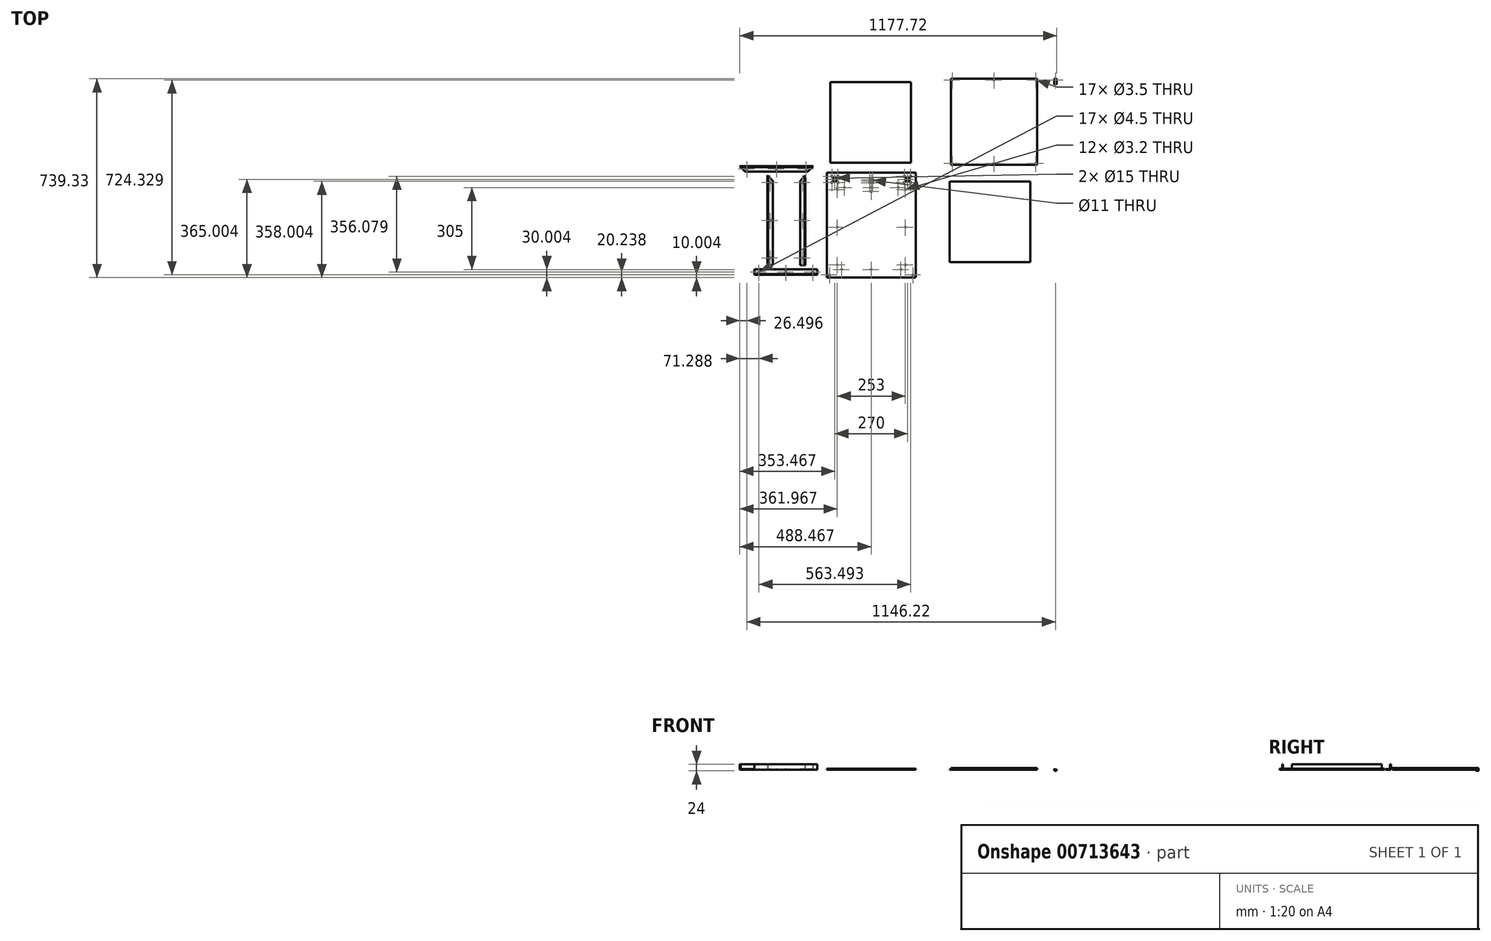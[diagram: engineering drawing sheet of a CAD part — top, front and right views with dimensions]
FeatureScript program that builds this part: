
annotation { "Feature Type Name" : "Feature", "Feature Type Description" : "" }
export const myFeature = defineFeature(function(context is Context, id is Id, definition is map)
    precondition{}
    {
        {
            var Q0;
            Q0=qCreatedBy(makeId("Top.planeOp"),FACE);
            var sketch = newSketch(context, id + "F0", { "sketchPlane" : qUnion([Q0])});
            skLineSegment(sketch, "E0.bottom", {"start": v(150, 187.33) * mm, "end": v(480, 187.33) * mm});
            skLineSegment(sketch, "E0.top", {"start": v(150, -202.67) * mm, "end": v(480, -202.67) * mm});
            skLineSegment(sketch, "E0.left", {"start": v(150, 187.33) * mm, "end": v(150, -202.67) * mm});
            skLineSegment(sketch, "E0.right", {"start": v(480, 187.33) * mm, "end": v(480, -202.67) * mm});
            skCircle(sketch, "E1", {"center": v(180, 162.33) * mm, "radius": 7.5 * mm});
            skCircle(sketch, "E2", {"center": v(450, 162.33) * mm, "radius": 7.5 * mm});
            skCircle(sketch, "E3", {"center": v(315, 155.33) * mm, "radius": 5.5 * mm});
            skPoint(sketch, "E3.centerSnap0", {"position": v(315, 187.33) * mm});
            skLineSegment(sketch, "E4", {"start": v(150, -202.67) * mm, "end": v(480, 187.33) * mm, "construction": true});
            skLineSegment(sketch, "E5.bottom", {"start": v(470, -192.67) * mm, "end": v(160, -192.67) * mm, "construction": true});
            skLineSegment(sketch, "E5.top", {"start": v(470, 117.33) * mm, "end": v(160, 117.33) * mm, "construction": true});
            skLineSegment(sketch, "E5.left", {"start": v(470, -192.67) * mm, "end": v(470, 117.33) * mm, "construction": true});
            skLineSegment(sketch, "E5.right", {"start": v(160, -192.67) * mm, "end": v(160, 117.33) * mm, "construction": true});
            skPoint(sketch, "E5.middle", {"position": v(315, -37.67) * mm});
            skCircle(sketch, "E6", {"center": v(315, 117.33) * mm, "radius": 1.75 * mm});
            skCircle(sketch, "E7", {"center": v(160, -192.67) * mm, "radius": 1.75 * mm});
            skCircle(sketch, "E8", {"center": v(470, -192.67) * mm, "radius": 1.75 * mm});
            skLineSegment(sketch, "E9", {"start": v(315, -7.67) * mm, "end": v(315, -37.67) * mm, "construction": true});
            skLineSegment(sketch, "E10", {"start": v(315, -37.67) * mm, "end": v(315, -37.67) * mm});
            skCircle(sketch, "E11", {"center": v(180, 162.33) * mm, "radius": 16 * mm, "construction": true});
            skCircle(sketch, "E12", {"center": v(168.7, 151.02) * mm, "radius": 2.25 * mm});
            skCircle(sketch, "E13", {"center": v(168.7, 173.65) * mm, "radius": 2.25 * mm});
            skCircle(sketch, "E14", {"center": v(191.32, 173.65) * mm, "radius": 2.25 * mm});
            skCircle(sketch, "E15", {"center": v(191.32, 151.02) * mm, "radius": 2.25 * mm});
            skLineSegment(sketch, "E16.bottom", {"start": v(168.7, 173.65) * mm, "end": v(191.32, 173.65) * mm, "construction": true});
            skLineSegment(sketch, "E16.top", {"start": v(168.7, 151.02) * mm, "end": v(191.32, 151.02) * mm, "construction": true});
            skLineSegment(sketch, "E16.left", {"start": v(168.7, 173.65) * mm, "end": v(168.7, 151.02) * mm, "construction": true});
            skLineSegment(sketch, "E16.right", {"start": v(191.32, 173.65) * mm, "end": v(191.32, 151.02) * mm, "construction": true});
            skCircle(sketch, "E17", {"center": v(450, 162.33) * mm, "radius": 16 * mm, "construction": true});
            skLineSegment(sketch, "E18.bottom", {"start": v(438.7, 173.65) * mm, "end": v(461.32, 173.65) * mm, "construction": true});
            skLineSegment(sketch, "E18.top", {"start": v(438.7, 151.02) * mm, "end": v(461.32, 151.02) * mm, "construction": true});
            skLineSegment(sketch, "E18.left", {"start": v(438.7, 173.65) * mm, "end": v(438.7, 151.02) * mm, "construction": true});
            skLineSegment(sketch, "E18.right", {"start": v(461.32, 173.65) * mm, "end": v(461.32, 151.02) * mm, "construction": true});
            skCircle(sketch, "E19", {"center": v(438.7, 173.65) * mm, "radius": 2.25 * mm});
            skCircle(sketch, "E20", {"center": v(461.32, 173.65) * mm, "radius": 2.25 * mm});
            skCircle(sketch, "E21", {"center": v(461.32, 151.02) * mm, "radius": 2.25 * mm});
            skCircle(sketch, "E22", {"center": v(438.7, 151.02) * mm, "radius": 2.25 * mm});
            skCircle(sketch, "E23", {"center": v(315, 155.33) * mm, "radius": 8 * mm, "construction": true});
            skLineSegment(sketch, "E24.bottom", {"start": v(309.35, 161) * mm, "end": v(320.66, 161) * mm, "construction": true});
            skLineSegment(sketch, "E24.top", {"start": v(309.35, 149.68) * mm, "end": v(320.66, 149.68) * mm, "construction": true});
            skLineSegment(sketch, "E24.left", {"start": v(309.35, 161) * mm, "end": v(309.35, 149.68) * mm, "construction": true});
            skLineSegment(sketch, "E24.right", {"start": v(320.66, 161) * mm, "end": v(320.66, 149.68) * mm, "construction": true});
            skCircle(sketch, "E25", {"center": v(309.35, 161) * mm, "radius": 1.75 * mm});
            skCircle(sketch, "E26", {"center": v(320.66, 161) * mm, "radius": 1.75 * mm});
            skCircle(sketch, "E27", {"center": v(320.66, 149.68) * mm, "radius": 1.75 * mm});
            skCircle(sketch, "E28", {"center": v(309.35, 149.68) * mm, "radius": 1.75 * mm});
            skCircle(sketch, "E29", {"center": v(188.5, -155.42) * mm, "radius": 1.6 * mm});
            skCircle(sketch, "E30", {"center": v(315, -172.67) * mm, "radius": 1.6 * mm});
            skPoint(sketch, "E30.centerSnap0", {"position": v(315, -202.67) * mm});
            skCircle(sketch, "E31", {"center": v(205, -172.67) * mm, "radius": 1.6 * mm});
            skCircle(sketch, "E32", {"center": v(425, -172.67) * mm, "radius": 1.6 * mm});
            skCircle(sketch, "E33", {"center": v(441.5, -155.42) * mm, "radius": 1.6 * mm});
            skCircle(sketch, "E34", {"center": v(188.5, -15.42) * mm, "radius": 1.6 * mm});
            skCircle(sketch, "E35", {"center": v(188.5, 124.58) * mm, "radius": 1.6 * mm});
            skCircle(sketch, "E36", {"center": v(441.5, -15.42) * mm, "radius": 1.6 * mm});
            skCircle(sketch, "E37", {"center": v(441.5, 124.58) * mm, "radius": 1.6 * mm});
            skCircle(sketch, "E38", {"center": v(315, 132.33) * mm, "radius": 1.6 * mm});
            skCircle(sketch, "E39", {"center": v(415, 132.33) * mm, "radius": 1.6 * mm});
            skCircle(sketch, "E40", {"center": v(215, 132.33) * mm, "radius": 1.6 * mm});
            skSolve(sketch);
        }
        {
            var Q0;
            Q0=makeQuery(id+"F0.imprint","IMPRINT",FACE,{"disambiguationData":[TD([[makeQuery(id+"F0.imprint","IMPRINT",EDGE,{"derivedFrom":sQuery(id+"F0.wireOp",EDGE,"E0.bottom")}),-1.0]])]});
            extrude(context, id + "F1", {"entities" : qUnion([Q0]), "depth" : 4 * mm});
        }
        {
            var Q0;
            Q0=qCreatedBy(makeId("Top.planeOp"),FACE);
            var sketch = newSketch(context, id + "F2", { "sketchPlane" : qUnion([Q0])});
            skLineSegment(sketch, "E41.bottom", {"start": v(605.69, 155) * mm, "end": v(905.69, 155) * mm});
            skLineSegment(sketch, "E41.top", {"start": v(605.69, -145) * mm, "end": v(905.69, -145) * mm});
            skLineSegment(sketch, "E41.left", {"start": v(605.69, 155) * mm, "end": v(605.69, -145) * mm});
            skLineSegment(sketch, "E41.right", {"start": v(905.69, 155) * mm, "end": v(905.69, -145) * mm});
            skSolve(sketch);
        }
        {
            var Q0;
            Q0=makeQuery(id+"F2.imprint","IMPRINT",FACE,{"disambiguationData":[TD([[makeQuery(id+"F2.imprint","IMPRINT",EDGE,{"derivedFrom":sQuery(id+"F2.wireOp",EDGE,"E41.bottom")}),-1.0]])]});
            extrude(context, id + "F3", {"entities" : qUnion([Q0]), "depth" : 2 * mm});
        }
        {
            var Q0;
            Q0=qCreatedBy(makeId("Top.planeOp"),FACE);
            var sketch = newSketch(context, id + "F4", { "sketchPlane" : qUnion([Q0])});
            skLineSegment(sketch, "E42.bottom", {"start": v(611.16, 536.66) * mm, "end": v(931.16, 536.66) * mm});
            skLineSegment(sketch, "E42.top", {"start": v(611.16, 216.66) * mm, "end": v(931.16, 216.66) * mm});
            skLineSegment(sketch, "E42.left", {"start": v(611.16, 536.66) * mm, "end": v(611.16, 216.66) * mm});
            skLineSegment(sketch, "E42.right", {"start": v(931.16, 536.66) * mm, "end": v(931.16, 216.66) * mm});
            skCircle(sketch, "E43", {"center": v(771.16, 531.66) * mm, "radius": 1.75 * mm});
            skPoint(sketch, "E43.centerSnap0", {"position": v(771.16, 536.66) * mm});
            skLineSegment(sketch, "E44", {"start": v(611.16, 216.66) * mm, "end": v(931.16, 536.66) * mm, "construction": true});
            skLineSegment(sketch, "E45", {"start": v(611.16, 536.66) * mm, "end": v(931.16, 216.66) * mm, "construction": true});
            skCircle(sketch, "E46", {"center": v(616.16, 221.66) * mm, "radius": 1.75 * mm});
            skCircle(sketch, "E47", {"center": v(926.16, 221.66) * mm, "radius": 1.75 * mm});
            skCircle(sketch, "E48", {"center": v(771.16, 221.66) * mm, "radius": 1.75 * mm});
            skPoint(sketch, "E48.centerSnap0", {"position": v(771.16, 216.66) * mm});
            skCircle(sketch, "E49", {"center": v(616.16, 531.66) * mm, "radius": 1.75 * mm});
            skCircle(sketch, "E50", {"center": v(926.16, 531.66) * mm, "radius": 1.75 * mm});
            skSolve(sketch);
        }
        {
            var Q0;
            Q0=makeQuery(id+"F4.imprint","IMPRINT",FACE,{"disambiguationData":[TD([[makeQuery(id+"F4.imprint","IMPRINT",EDGE,{"derivedFrom":sQuery(id+"F4.wireOp",EDGE,"E42.bottom")}),-1.0]])]});
            extrude(context, id + "F5", {"entities" : qUnion([Q0]), "depth" : 6 * mm});
        }
        {
            var Q0;
            Q0=qCreatedBy(makeId("Top.planeOp"),FACE);
            var sketch = newSketch(context, id + "F6", { "sketchPlane" : qUnion([Q0])});
            skLineSegment(sketch, "E51.bottom", {"start": v(162.3, 524.65) * mm, "end": v(462.3, 524.65) * mm});
            skLineSegment(sketch, "E51.top", {"start": v(162.3, 224.65) * mm, "end": v(462.3, 224.65) * mm});
            skLineSegment(sketch, "E51.left", {"start": v(162.3, 524.65) * mm, "end": v(162.3, 224.65) * mm});
            skLineSegment(sketch, "E51.right", {"start": v(462.3, 524.65) * mm, "end": v(462.3, 224.65) * mm});
            skSolve(sketch);
        }
        {
            var Q0;
            Q0=qSketchRegion(id+"F6",true);
            extrude(context, id + "F7", {"entities" : qUnion([Q0]), "depth" : 4 * mm});
        }
        {
            var Q0;
            Q0=qCreatedBy(makeId("Top.planeOp"),FACE);
            var sketch = newSketch(context, id + "F8", { "sketchPlane" : qUnion([Q0])});
            skCircle(sketch, "E52", {"center": v(999.26, 531.22) * mm, "radius": 1.75 * mm});
            skCircle(sketch, "E53", {"center": v(999.26, 531.22) * mm, "radius": 5 * mm});
            skLineSegment(sketch, "E54.bottom", {"start": v(994.26, 536.22) * mm, "end": v(1004.26, 536.22) * mm});
            skLineSegment(sketch, "E54.top", {"start": v(994.26, 516.22) * mm, "end": v(1004.26, 516.22) * mm});
            skLineSegment(sketch, "E54.left", {"start": v(994.26, 536.22) * mm, "end": v(994.26, 516.22) * mm});
            skLineSegment(sketch, "E54.right", {"start": v(1004.26, 536.22) * mm, "end": v(1004.26, 516.22) * mm});
            skSolve(sketch);
        }
        {
            var Q0;
            Q0=makeQuery(id+"F8.imprint","IMPRINT",FACE,{"disambiguationData":[TD([[makeQuery(id+"F8.imprint","IMPRINT",EDGE,{"derivedFrom":sQuery(id+"F8.wireOp",EDGE,"E52")}),-1.0]])]});
            var Q1;
            {var subQ0=sQuery(id+"F8.wireOp",EDGE,"E54.bottom");var subQ1=sQuery(id+"F8.wireOp",EDGE,"E53");var subQ2=makeQuery(id+"F8.imprint","INTERSECT",VERTEX,{"derivedFrom":[subQ1,subQ0]});Q1=makeQuery(id+"F8.imprint","IMPRINT",FACE,{"disambiguationData":[TD([[makeQuery(id+"F8.imprint","IMPRINT",EDGE,{"disambiguationData":[TD([[subQ2,-1.0]])],"derivedFrom":subQ1}),-1.0]])]});}
            var Q2;
            {var subQ0=sQuery(id+"F8.wireOp",EDGE,"E54.bottom");var subQ1=sQuery(id+"F8.wireOp",EDGE,"E53");var subQ2=makeQuery(id+"F8.imprint","INTERSECT",VERTEX,{"derivedFrom":[subQ1,subQ0]});Q2=makeQuery(id+"F8.imprint","IMPRINT",FACE,{"disambiguationData":[TD([[makeQuery(id+"F8.imprint","IMPRINT",EDGE,{"disambiguationData":[TD([[subQ2,1.0]])],"derivedFrom":subQ1}),-1.0]])]});}
            extrude(context, id + "F9", {"entities" : qUnion([Q0, Q1, Q2]), "oppositeDirection" : true, "depth" : 4 * mm});
        }
        {
            var Q0;
            Q0=qSketchRegion(id+"F8",true);
            extrude(context, id + "F10", {"entities" : qUnion([Q0]), "operationType" : NewBodyOperationType.ADD, "depth" : 2 * mm});
        }
        {
            var Q0;
            Q0=makeQuery(id+"F10.opExtrude","SWEPT_EDGE",EDGE,{"disambiguationData":[OSD([sQuery(id+"F8.wireOp",EDGE,"E54.top"),sQuery(id+"F8.wireOp",EDGE,"E54.left")])]});
            var Q1;
            Q1=makeQuery(id+"F10.opExtrude","SWEPT_EDGE",EDGE,{"disambiguationData":[OSD([sQuery(id+"F8.wireOp",EDGE,"E54.top"),sQuery(id+"F8.wireOp",EDGE,"E54.right")])]});
            var Q2;
            {var subQ0=sQuery(id+"F8.wireOp",EDGE,"E54.right");var subQ1=sQuery(id+"F8.wireOp",EDGE,"E54.bottom");Q2=makeQuery(id+"F10.boolean.opBoolean","MERGE",EDGE,{"derivedFrom":[makeQuery(id+"F9.opExtrude","SWEPT_EDGE",EDGE,{"disambiguationData":[OSD([subQ1,subQ0])]}),makeQuery(id+"F10.opExtrude","SWEPT_EDGE",EDGE,{"disambiguationData":[OSD([subQ1,subQ0])]})]});}
            var Q3;
            {var subQ0=sQuery(id+"F8.wireOp",EDGE,"E54.left");var subQ1=sQuery(id+"F8.wireOp",EDGE,"E54.bottom");Q3=makeQuery(id+"F10.boolean.opBoolean","MERGE",EDGE,{"derivedFrom":[makeQuery(id+"F9.opExtrude","SWEPT_EDGE",EDGE,{"disambiguationData":[OSD([subQ1,subQ0])]}),makeQuery(id+"F10.opExtrude","SWEPT_EDGE",EDGE,{"disambiguationData":[OSD([subQ1,subQ0])]})]});}
            fillet(context, id + "F11", {"entities" : qUnion([Q0, Q1, Q2, Q3]), "radius" : 2 * mm, "tangentPropagation" : true, "allowEdgeOverflow" : false});
        }
        {
            var Q0;
            Q0=qCreatedBy(makeId("Top.planeOp"),FACE);
            var sketch = newSketch(context, id + "F12", { "sketchPlane" : qUnion([Q0])});
            skLineSegment(sketch, "E55.bottom", {"start": v(-70.66, 177.44) * mm, "end": v(-50.66, 177.44) * mm});
            skLineSegment(sketch, "E55.top", {"start": v(-70.66, -157.06) * mm, "end": v(-50.66, -157.06) * mm});
            skLineSegment(sketch, "E55.left", {"start": v(-70.66, 177.44) * mm, "end": v(-70.66, -157.06) * mm});
            skLineSegment(sketch, "E55.right", {"start": v(-50.66, 177.44) * mm, "end": v(-50.66, -157.06) * mm});
            skLineSegment(sketch, "E56", {"start": v(-70.66, 177.44) * mm, "end": v(-50.66, 157.44) * mm});
            skCircle(sketch, "E57", {"center": v(-60.66, -129.8) * mm, "radius": 2.25 * mm});
            skPoint(sketch, "E57.centerSnap0", {"position": v(-60.66, -157.06) * mm});
            skCircle(sketch, "E58", {"center": v(-60.66, 10.2) * mm, "radius": 2.25 * mm});
            skPoint(sketch, "E58.centerSnap0", {"position": v(-50.66, 10.2) * mm});
            skCircle(sketch, "E59", {"center": v(-60.66, 150.2) * mm, "radius": 2.25 * mm});
            skPoint(sketch, "E59.centerSnap0", {"position": v(-60.66, 167.44) * mm});
            skSolve(sketch);
        }
        {
            var Q0;
            {var subQ0=sQuery(id+"F12.wireOp",EDGE,"E55.top");Q0=makeQuery(id+"F12.imprint","IMPRINT",FACE,{"disambiguationData":[TD([[makeQuery(id+"F12.imprint","IMPRINT",EDGE,{"derivedFrom":subQ0}),1.0]])]});}
            extrude(context, id + "F13", {"entities" : qUnion([Q0]), "depth" : 3 * mm});
        }
        {
            var Q0;
            Q0=makeQuery(id+"F13.opExtrude","CAP_FACE",FACE,{"disambiguationData":[OSD([sQuery(id+"F12.wireOp",EDGE,"E55.top"),sQuery(id+"F12.wireOp",EDGE,"E55.left"),sQuery(id+"F12.wireOp",EDGE,"E55.right"),sQuery(id+"F12.wireOp",EDGE,"E56")])],"isStart":true});
            var sketch = newSketch(context, id + "F14", { "sketchPlane" : qUnion([Q0])});
            skLineSegment(sketch, "E60", {"start": v(-70.66, -177.44) * mm, "end": v(-70.66, 157.06) * mm});
            skLineSegment(sketch, "E61", {"start": v(-70.66, 157.06) * mm, "end": v(-67.66, 157.06) * mm});
            skLineSegment(sketch, "E62", {"start": v(-67.66, 157.06) * mm, "end": v(-67.66, -174.44) * mm});
            skLineSegment(sketch, "E63", {"start": v(-67.66, -174.44) * mm, "end": v(-70.66, -177.44) * mm});
            skSolve(sketch);
        }
        {
            var Q0;
            Q0=makeQuery(id+"F14.imprint","IMPRINT",FACE,{"disambiguationData":[TD([[makeQuery(id+"F14.imprint","IMPRINT",EDGE,{"derivedFrom":sQuery(id+"F14.wireOp",EDGE,"E60")}),-1.0]])]});
            extrude(context, id + "F15", {"entities" : qUnion([Q0]), "operationType" : NewBodyOperationType.ADD, "oppositeDirection" : true, "depth" : 20 * mm});
        }
        {
            var Q0;
            Q0=makeQuery(id+"F13.opExtrude","SWEPT_BODY",BODY,{"disambiguationData":[OSD([sQuery(id+"F12.wireOp",EDGE,"E55.top"),sQuery(id+"F12.wireOp",EDGE,"E55.left"),sQuery(id+"F12.wireOp",EDGE,"E55.right"),sQuery(id+"F12.wireOp",EDGE,"E56"),sQuery(id+"F12.wireOp",EDGE,"E57"),sQuery(id+"F12.wireOp",EDGE,"E58"),sQuery(id+"F12.wireOp",EDGE,"E59")])]});
            var Q1;
            Q1=qCreatedBy(makeId("Right.planeOp"),FACE);
            mirror(context, id + "F16", {"entities" : qUnion([Q0]), "mirrorPlane" : qUnion([Q1])});
        }
        {
            var Q0;
            Q0=qCreatedBy(makeId("Top.planeOp"),FACE);
            var sketch = newSketch(context, id + "F17", { "sketchPlane" : qUnion([Q0])});
            skLineSegment(sketch, "E64.bottom", {"start": v(-173.46, 211.15) * mm, "end": v(99.54, 211.15) * mm});
            skLineSegment(sketch, "E64.top", {"start": v(-173.46, 191.15) * mm, "end": v(99.54, 191.15) * mm});
            skLineSegment(sketch, "E64.left", {"start": v(-173.46, 211.15) * mm, "end": v(-173.46, 191.15) * mm});
            skLineSegment(sketch, "E64.right", {"start": v(99.54, 211.15) * mm, "end": v(99.54, 191.15) * mm});
            skLineSegment(sketch, "E65", {"start": v(-173.46, 211.15) * mm, "end": v(-153.46, 191.15) * mm});
            skLineSegment(sketch, "E66", {"start": v(99.54, 211.15) * mm, "end": v(79.54, 191.15) * mm});
            skCircle(sketch, "E67", {"center": v(-146.96, 201.15) * mm, "radius": 1.75 * mm});
            skPoint(sketch, "E67.centerSnap0", {"position": v(-163.46, 201.15) * mm});
            skCircle(sketch, "E68", {"center": v(-36.96, 201.15) * mm, "radius": 1.75 * mm});
            skPoint(sketch, "E68.centerSnap0", {"position": v(-36.96, 191.15) * mm});
            skCircle(sketch, "E69", {"center": v(73.04, 201.15) * mm, "radius": 1.75 * mm});
            skPoint(sketch, "E69.centerSnap0", {"position": v(89.54, 201.15) * mm});
            skSolve(sketch);
        }
        {
            var Q0;
            Q0=makeQuery(id+"F17.imprint","IMPRINT",FACE,{"disambiguationData":[TD([[makeQuery(id+"F17.imprint","IMPRINT",EDGE,{"derivedFrom":sQuery(id+"F17.wireOp",EDGE,"E64.bottom")}),-1.0]])]});
            extrude(context, id + "F18", {"entities" : qUnion([Q0]), "depth" : 3 * mm});
        }
        {
            var Q0;
            Q0=makeQuery(id+"F18.opExtrude","CAP_FACE",FACE,{"disambiguationData":[OSD([sQuery(id+"F17.wireOp",EDGE,"E64.bottom"),sQuery(id+"F17.wireOp",EDGE,"E64.top"),sQuery(id+"F17.wireOp",EDGE,"E65"),sQuery(id+"F17.wireOp",EDGE,"E66")])],"isStart":true});
            var sketch = newSketch(context, id + "F19", { "sketchPlane" : qUnion([Q0])});
            skLineSegment(sketch, "E70", {"start": v(-173.46, -211.15) * mm, "end": v(99.54, -211.15) * mm});
            skLineSegment(sketch, "E71", {"start": v(99.54, -211.15) * mm, "end": v(96.54, -208.15) * mm});
            skLineSegment(sketch, "E72", {"start": v(96.54, -208.15) * mm, "end": v(-170.46, -208.15) * mm});
            skLineSegment(sketch, "E73", {"start": v(-170.46, -208.15) * mm, "end": v(-173.46, -211.15) * mm});
            skSolve(sketch);
        }
        {
            var Q0;
            Q0=qSketchRegion(id+"F19",true);
            extrude(context, id + "F20", {"entities" : qUnion([Q0]), "operationType" : NewBodyOperationType.ADD, "oppositeDirection" : true, "depth" : 20 * mm});
        }
        {
            var Q0;
            Q0=qCreatedBy(makeId("Top.planeOp"),FACE);
            var sketch = newSketch(context, id + "F21", { "sketchPlane" : qUnion([Q0])});
            skLineSegment(sketch, "E74.bottom", {"start": v(-118.67, -172.43) * mm, "end": v(114.33, -172.43) * mm});
            skLineSegment(sketch, "E74.top", {"start": v(-118.67, -192.43) * mm, "end": v(114.33, -192.43) * mm});
            skLineSegment(sketch, "E74.left", {"start": v(-118.67, -172.43) * mm, "end": v(-118.67, -192.43) * mm});
            skLineSegment(sketch, "E74.right", {"start": v(114.33, -172.43) * mm, "end": v(114.33, -192.43) * mm});
            skCircle(sketch, "E75", {"center": v(-102.17, -182.43) * mm, "radius": 2.25 * mm});
            skPoint(sketch, "E75.centerSnap0", {"position": v(-118.67, -182.43) * mm});
            skCircle(sketch, "E76", {"center": v(-2.17, -182.43) * mm, "radius": 2.25 * mm});
            skPoint(sketch, "E76.centerSnap0", {"position": v(-2.17, -172.43) * mm});
            skCircle(sketch, "E77", {"center": v(97.83, -182.43) * mm, "radius": 2.25 * mm});
            skLineSegment(sketch, "E78", {"start": v(-118.67, -189.43) * mm, "end": v(114.33, -189.43) * mm});
            skSolve(sketch);
        }
        {
            var Q0;
            Q0=qSketchRegion(id+"F21",true);
            extrude(context, id + "F22", {"entities" : qUnion([Q0]), "depth" : 3 * mm});
        }
        {
            var Q0;
            {var subQ0=sQuery(id+"F21.wireOp",EDGE,"E74.top");Q0=makeQuery(id+"F21.imprint","IMPRINT",FACE,{"disambiguationData":[TD([[makeQuery(id+"F21.imprint","IMPRINT",EDGE,{"derivedFrom":subQ0}),1.0]])]});}
            extrude(context, id + "F23", {"entities" : qUnion([Q0]), "operationType" : NewBodyOperationType.ADD, "depth" : 20 * mm});
        }
    });
